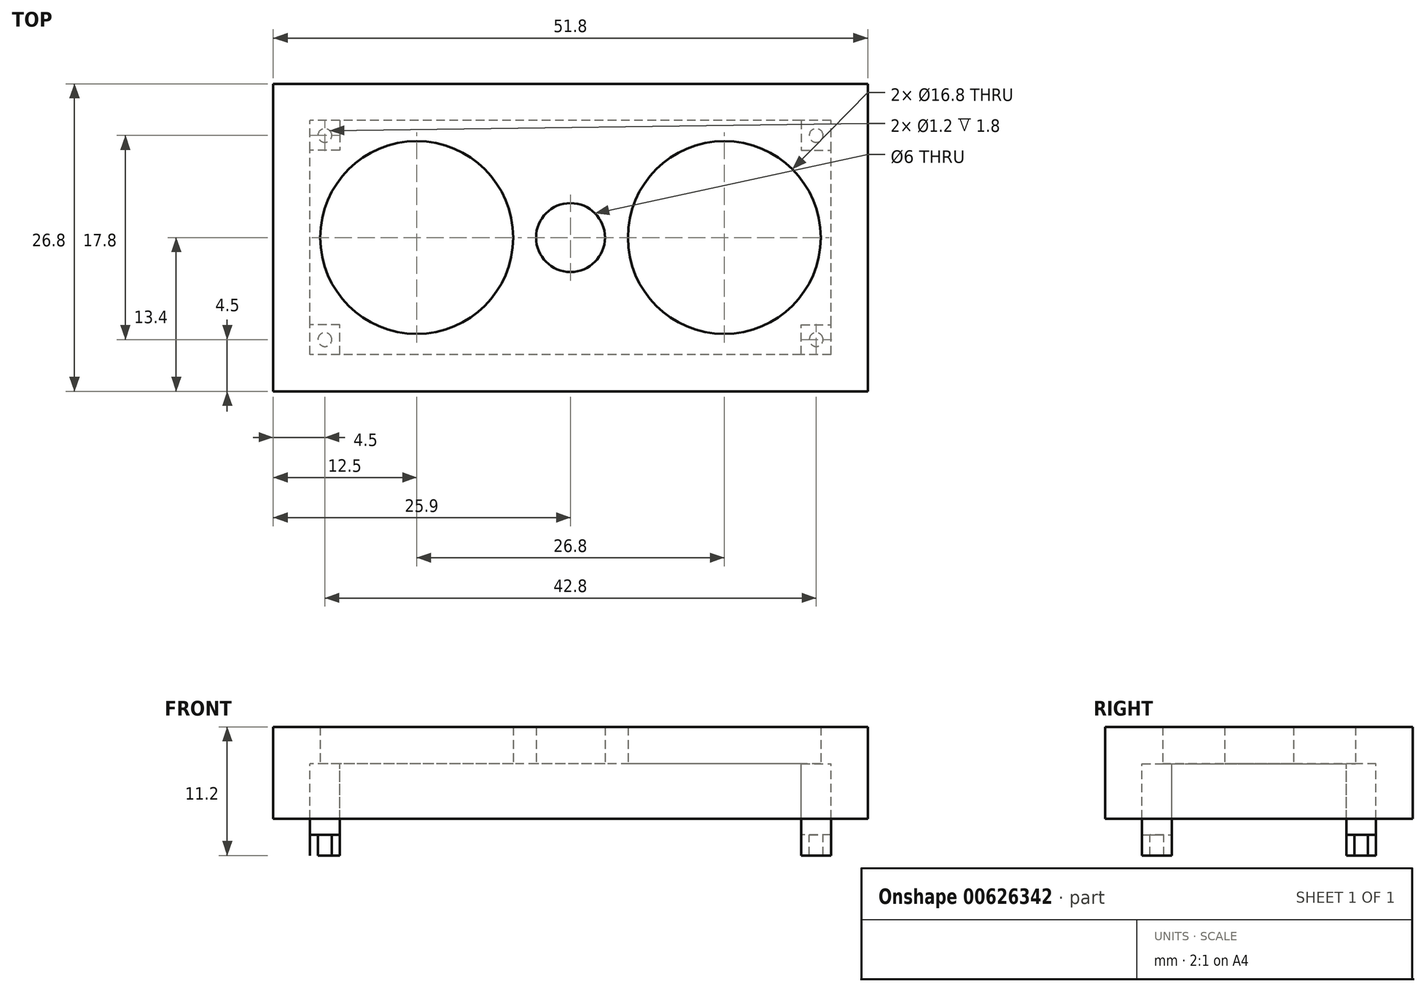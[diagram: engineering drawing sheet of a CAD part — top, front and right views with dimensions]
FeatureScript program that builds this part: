
annotation { "Feature Type Name" : "Feature", "Feature Type Description" : "" }
export const myFeature = defineFeature(function(context is Context, id is Id, definition is map)
    precondition{}
    {
        {
            var Q0;
            Q0=qCreatedBy(makeId("Top.planeOp"),FACE);
            var sketch = newSketch(context, id + "F0", { "sketchPlane" : qUnion([Q0])});
            skLineSegment(sketch, "E0.bottom", {"start": v(0, 0) * mm, "end": v(-22.7, 0) * mm});
            skLineSegment(sketch, "E0.top", {"start": v(0, 10.2) * mm, "end": v(-22.7, 10.2) * mm});
            skLineSegment(sketch, "E0.left", {"start": v(0, 0) * mm, "end": v(0, 10.2) * mm});
            skLineSegment(sketch, "E0.right", {"start": v(-22.7, 0) * mm, "end": v(-22.7, 10.2) * mm});
            skLineSegment(sketch, "E1.MirrorCS", {"start": v(-22.7, 0) * mm, "end": v(-22.7, -10.2) * mm});
            skLineSegment(sketch, "E2.MirrorCS", {"start": v(0, 0) * mm, "end": v(0, -10.2) * mm});
            skLineSegment(sketch, "E3.MirrorCS", {"start": v(0, -10.2) * mm, "end": v(-22.7, -10.2) * mm});
            skLineSegment(sketch, "E4", {"start": v(-5, 0) * mm, "end": v(-5, 10.2) * mm, "construction": true});
            skCircle(sketch, "E5", {"center": v(-13.4, 0) * mm, "radius": 8.4 * mm});
            skLineSegment(sketch, "E6.MirrorCS", {"start": v(0, 10.2) * mm, "end": v(22.7, 10.2) * mm});
            skCircle(sketch, "E7.MirrorC", {"center": v(13.4, 0) * mm, "radius": 8.4 * mm});
            skLineSegment(sketch, "E8.MirrorCS", {"start": v(0, -10.2) * mm, "end": v(22.7, -10.2) * mm});
            skLineSegment(sketch, "E9.MirrorCS", {"start": v(22.7, 0) * mm, "end": v(22.7, 10.2) * mm});
            skLineSegment(sketch, "E10.MirrorCS", {"start": v(0, 0) * mm, "end": v(22.7, 0) * mm});
            skLineSegment(sketch, "E11.MirrorCS", {"start": v(22.7, 0) * mm, "end": v(22.7, -10.2) * mm});
            skLineSegment(sketch, "E12.MirrorCS", {"start": v(5, 0) * mm, "end": v(5, 10.2) * mm, "construction": true});
            skCircle(sketch, "E13", {"center": v(0, 0) * mm, "radius": 3 * mm});
            skSolve(sketch);
        }
        {
            var Q0;
            {var subQ1=sQuery(id+"F0.wireOp",EDGE,"E0.top");Q0=makeQuery(id+"F0.imprint","IMPRINT",FACE,{"disambiguationData":[TD([[makeQuery(id+"F0.imprint","IMPRINT",EDGE,{"derivedFrom":subQ1}),1.0]])]});}
            var Q1;
            {var subQ1=sQuery(id+"F0.wireOp",EDGE,"E1.MirrorCS");Q1=makeQuery(id+"F0.imprint","IMPRINT",FACE,{"disambiguationData":[TD([[makeQuery(id+"F0.imprint","IMPRINT",EDGE,{"derivedFrom":subQ1}),1.0]])]});}
            var Q2;
            {var subQ7=sQuery(id+"F0.wireOp",EDGE,"E6.MirrorCS");Q2=makeQuery(id+"F0.imprint","IMPRINT",FACE,{"disambiguationData":[TD([[makeQuery(id+"F0.imprint","IMPRINT",EDGE,{"derivedFrom":subQ7}),-1.0]])]});}
            var Q3;
            {var subQ9=sQuery(id+"F0.wireOp",EDGE,"E8.MirrorCS");Q3=makeQuery(id+"F0.imprint","IMPRINT",FACE,{"disambiguationData":[TD([[makeQuery(id+"F0.imprint","IMPRINT",EDGE,{"derivedFrom":subQ9}),1.0]])]});}
            extrude(context, id + "F1", {"entities" : qUnion([Q0, Q1, Q2, Q3]), "endBound" : BoundingType.SYMMETRIC, "depth" : 3.2 * mm, "offsetDistance" : 25 * mm});
        }
        {
            var Q0;
            Q0=makeQuery(id+"F1.opExtrude","CAP_FACE",FACE,{"disambiguationData":[OSD([sQuery(id+"F0.wireOp",EDGE,"E0.top"),sQuery(id+"F0.wireOp",EDGE,"E0.right"),sQuery(id+"F0.wireOp",EDGE,"E1.MirrorCS"),sQuery(id+"F0.wireOp",EDGE,"E3.MirrorCS"),sQuery(id+"F0.wireOp",EDGE,"E5"),sQuery(id+"F0.wireOp",EDGE,"E6.MirrorCS"),sQuery(id+"F0.wireOp",EDGE,"E7.MirrorC"),sQuery(id+"F0.wireOp",EDGE,"E8.MirrorCS"),sQuery(id+"F0.wireOp",EDGE,"E9.MirrorCS"),sQuery(id+"F0.wireOp",EDGE,"E11.MirrorCS"),sQuery(id+"F0.wireOp",EDGE,"E13")])],"isStart":false});
            var sketch = newSketch(context, id + "F2", { "sketchPlane" : qUnion([Q0])});
            skLineSegment(sketch, "E14.0", {"start": v(22.7, 10.2) * mm, "end": v(-22.7, 10.2) * mm});
            skLineSegment(sketch, "E14.1", {"start": v(-22.7, -10.2) * mm, "end": v(-22.7, 10.2) * mm});
            skLineSegment(sketch, "E14.2", {"start": v(22.7, -10.2) * mm, "end": v(-22.7, -10.2) * mm});
            skLineSegment(sketch, "E14.3", {"start": v(22.7, -10.2) * mm, "end": v(22.7, 10.2) * mm});
            skPoint(sketch, "E14.4", {"position": v(0, 0) * mm});
            skLineSegment(sketch, "E15.bottom", {"start": v(0, 13.4) * mm, "end": v(-25.9, 13.4) * mm});
            skLineSegment(sketch, "E15.top", {"start": v(0, -13.4) * mm, "end": v(-25.9, -13.4) * mm});
            skLineSegment(sketch, "E15.left", {"start": v(0, 13.4) * mm, "end": v(0, -13.4) * mm});
            skLineSegment(sketch, "E15.right", {"start": v(-25.9, 13.4) * mm, "end": v(-25.9, -13.4) * mm});
            skLineSegment(sketch, "E16.MirrorCS", {"start": v(0, 13.4) * mm, "end": v(25.9, 13.4) * mm});
            skLineSegment(sketch, "E17.MirrorCS", {"start": v(25.9, 13.4) * mm, "end": v(25.9, -13.4) * mm});
            skLineSegment(sketch, "E18.MirrorCS", {"start": v(0, -13.4) * mm, "end": v(25.9, -13.4) * mm});
            skSolve(sketch);
        }
        {
            var Q0;
            {var subQ1=sQuery(id+"F2.wireOp",EDGE,"E14.1");Q0=makeQuery(id+"F2.imprint","IMPRINT",FACE,{"disambiguationData":[TD([[makeQuery(id+"F2.imprint","IMPRINT",EDGE,{"derivedFrom":subQ1}),1.0]])]});}
            var Q1;
            {var subQ4=sQuery(id+"F2.wireOp",EDGE,"E14.3");Q1=makeQuery(id+"F2.imprint","IMPRINT",FACE,{"disambiguationData":[TD([[makeQuery(id+"F2.imprint","IMPRINT",EDGE,{"derivedFrom":subQ4}),-1.0]])]});}
            extrude(context, id + "F3", {"entities" : qUnion([Q0, Q1]), "operationType" : NewBodyOperationType.ADD, "oppositeDirection" : true, "depth" : 8 * mm, "offsetDistance" : 25 * mm});
        }
        {
            var Q0;
            Q0=makeQuery(id+"F1.opExtrude","CAP_FACE",FACE,{"disambiguationData":[OSD([sQuery(id+"F0.wireOp",EDGE,"E0.top"),sQuery(id+"F0.wireOp",EDGE,"E0.right"),sQuery(id+"F0.wireOp",EDGE,"E1.MirrorCS"),sQuery(id+"F0.wireOp",EDGE,"E3.MirrorCS"),sQuery(id+"F0.wireOp",EDGE,"E5"),sQuery(id+"F0.wireOp",EDGE,"E6.MirrorCS"),sQuery(id+"F0.wireOp",EDGE,"E7.MirrorC"),sQuery(id+"F0.wireOp",EDGE,"E8.MirrorCS"),sQuery(id+"F0.wireOp",EDGE,"E9.MirrorCS"),sQuery(id+"F0.wireOp",EDGE,"E11.MirrorCS"),sQuery(id+"F0.wireOp",EDGE,"E13")])],"isStart":true});
            var sketch = newSketch(context, id + "F4", { "sketchPlane" : qUnion([Q0])});
            skLineSegment(sketch, "E19.0", {"start": v(22.7, 10.2) * mm, "end": v(-22.7, 10.2) * mm});
            skLineSegment(sketch, "E19.1", {"start": v(-22.7, 10.2) * mm, "end": v(-22.7, -10.2) * mm});
            skLineSegment(sketch, "E19.2", {"start": v(22.7, -10.2) * mm, "end": v(-22.7, -10.2) * mm});
            skLineSegment(sketch, "E19.3", {"start": v(22.7, 10.2) * mm, "end": v(22.7, -10.2) * mm});
            skLineSegment(sketch, "E20", {"start": v(-21.4, 10.2) * mm, "end": v(-21.4, 8.9) * mm, "construction": true});
            skLineSegment(sketch, "E21", {"start": v(-21.4, 8.9) * mm, "end": v(-22.7, 8.9) * mm, "construction": true});
            skCircle(sketch, "E22", {"center": v(-21.4, 8.9) * mm, "radius": 0.6 * mm});
            skCircle(sketch, "E23.MirrorC", {"center": v(-21.4, -8.9) * mm, "radius": 0.6 * mm});
            skCircle(sketch, "E24.MirrorC", {"center": v(21.4, 8.9) * mm, "radius": 0.6 * mm});
            skCircle(sketch, "E25.MirrorC", {"center": v(21.4, -8.9) * mm, "radius": 0.6 * mm});
            skLineSegment(sketch, "E26.bottom", {"start": v(-20.1, 10.2) * mm, "end": v(-22.7, 10.2) * mm});
            skLineSegment(sketch, "E26.top", {"start": v(-20.1, 7.6) * mm, "end": v(-22.7, 7.6) * mm});
            skLineSegment(sketch, "E26.left", {"start": v(-20.1, 10.2) * mm, "end": v(-20.1, 7.6) * mm});
            skLineSegment(sketch, "E26.right", {"start": v(-22.7, 10.2) * mm, "end": v(-22.7, 7.6) * mm});
            skLineSegment(sketch, "E27.MirrorCS", {"start": v(20.1, 10.2) * mm, "end": v(20.1, 7.6) * mm});
            skLineSegment(sketch, "E28.MirrorCS", {"start": v(20.1, 7.6) * mm, "end": v(22.7, 7.6) * mm});
            skLineSegment(sketch, "E29.MirrorCS", {"start": v(20.1, -7.6) * mm, "end": v(22.7, -7.6) * mm});
            skLineSegment(sketch, "E30.MirrorCS", {"start": v(20.1, -10.2) * mm, "end": v(20.1, -7.6) * mm});
            skLineSegment(sketch, "E31.MirrorCS", {"start": v(-20.1, -10.2) * mm, "end": v(-20.1, -7.6) * mm});
            skLineSegment(sketch, "E32.MirrorCS", {"start": v(-20.1, -7.6) * mm, "end": v(-22.7, -7.6) * mm});
            skSolve(sketch);
        }
        {
            var Q0;
            Q0=makeQuery(id+"F4.imprint","IMPRINT",FACE,{"disambiguationData":[TD([[makeQuery(id+"F4.imprint","IMPRINT",EDGE,{"derivedFrom":sQuery(id+"F4.wireOp",EDGE,"E22")}),1.0]])]});
            var Q1;
            Q1=makeQuery(id+"F4.imprint","IMPRINT",FACE,{"disambiguationData":[TD([[makeQuery(id+"F4.imprint","IMPRINT",EDGE,{"derivedFrom":sQuery(id+"F4.wireOp",EDGE,"E23.MirrorC")}),-1.0]])]});
            var Q2;
            Q2=makeQuery(id+"F4.imprint","IMPRINT",FACE,{"disambiguationData":[TD([[makeQuery(id+"F4.imprint","IMPRINT",EDGE,{"derivedFrom":sQuery(id+"F4.wireOp",EDGE,"E25.MirrorC")}),1.0]])]});
            var Q3;
            Q3=makeQuery(id+"F4.imprint","IMPRINT",FACE,{"disambiguationData":[TD([[makeQuery(id+"F4.imprint","IMPRINT",EDGE,{"derivedFrom":sQuery(id+"F4.wireOp",EDGE,"E24.MirrorC")}),-1.0]])]});
            extrude(context, id + "F5", {"entities" : qUnion([Q0, Q1, Q2, Q3]), "operationType" : NewBodyOperationType.ADD, "depth" : 8 * mm, "offsetDistance" : 25 * mm});
        }
        {
            var Q0;
            Q0=makeQuery(id+"F4.imprint","IMPRINT",FACE,{"disambiguationData":[TD([[makeQuery(id+"F4.imprint","IMPRINT",EDGE,{"derivedFrom":sQuery(id+"F4.wireOp",EDGE,"E22")}),-1.0]])]});
            var Q1;
            Q1=makeQuery(id+"F4.imprint","IMPRINT",FACE,{"disambiguationData":[TD([[makeQuery(id+"F4.imprint","IMPRINT",EDGE,{"derivedFrom":sQuery(id+"F4.wireOp",EDGE,"E23.MirrorC")}),1.0]])]});
            var Q2;
            Q2=makeQuery(id+"F4.imprint","IMPRINT",FACE,{"disambiguationData":[TD([[makeQuery(id+"F4.imprint","IMPRINT",EDGE,{"derivedFrom":sQuery(id+"F4.wireOp",EDGE,"E24.MirrorC")}),1.0]])]});
            var Q3;
            Q3=makeQuery(id+"F4.imprint","IMPRINT",FACE,{"disambiguationData":[TD([[makeQuery(id+"F4.imprint","IMPRINT",EDGE,{"derivedFrom":sQuery(id+"F4.wireOp",EDGE,"E25.MirrorC")}),-1.0]])]});
            extrude(context, id + "F6", {"entities" : qUnion([Q0, Q1, Q2, Q3]), "operationType" : NewBodyOperationType.ADD, "depth" : 6.2 * mm, "offsetDistance" : 25 * mm});
        }
    });
